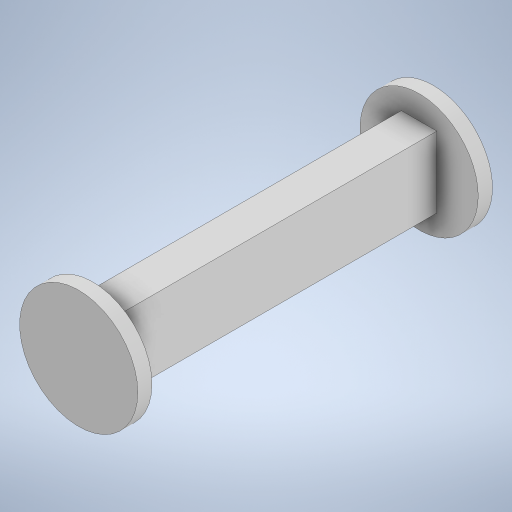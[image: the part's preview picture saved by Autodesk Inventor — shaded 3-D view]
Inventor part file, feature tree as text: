
AUTODESK INVENTOR PART (.ipt)
format: ipt  version: 2023 (Build 270158000, 158)  size: 255,488 bytes
history: native  units: mm
features: extrude x7, sketch x7, other x1
ambient origin geometry x8: Origin, YZ Plane, XZ Plane, XY Plane, X Axis, Y Axis, Z Axis, Center Point
bodies: Body1 (feature_tree)
feature tree (15):
  other  "ソリッド1"
  extrude  "押し出し1"  Depth=50.0mm
  extrude  "押し出し2"  Depth=6.0mm TaperAngle=0.0deg
  extrude  "押し出し3"  Depth=15.0mm
  extrude  "押し出し4"  Depth=30.0mm
  extrude  "押し出し5"  Depth=7.5mm
  extrude  "押し出し6"  Depth=15.0mm
  extrude  "押し出し7"  Depth=100.0mm TaperAngle=0.0deg
  sketch  "スケッチ1"
  sketch  "スケッチ2"
  sketch  "スケッチ3"
  sketch  "スケッチ4"
  sketch  "スケッチ5"
  sketch  "スケッチ6"
  sketch  "スケッチ7"
